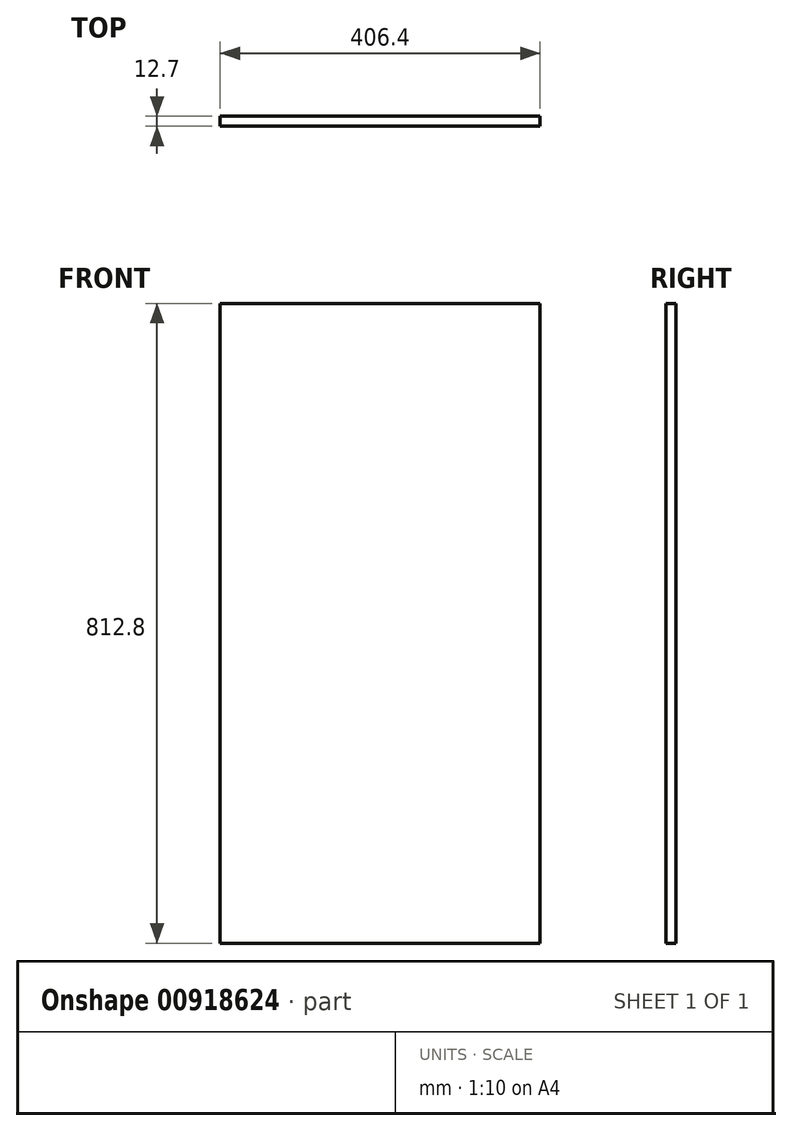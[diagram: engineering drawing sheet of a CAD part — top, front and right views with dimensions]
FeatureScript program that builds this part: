
annotation { "Feature Type Name" : "Feature", "Feature Type Description" : "" }
export const myFeature = defineFeature(function(context is Context, id is Id, definition is map)
    precondition{}
    {
        {
            var Q0;
            Q0=qCreatedBy(makeId("Front.planeOp"),FACE);
            var sketch = newSketch(context, id + "F0", { "sketchPlane" : qUnion([Q0])});
            skLineSegment(sketch, "E0.bottom", {"start": v(-203.2, 406.4) * mm, "end": v(203.2, 406.4) * mm});
            skLineSegment(sketch, "E0.top", {"start": v(-203.2, -406.4) * mm, "end": v(203.2, -406.4) * mm});
            skLineSegment(sketch, "E0.left", {"start": v(-203.2, 406.4) * mm, "end": v(-203.2, -406.4) * mm});
            skLineSegment(sketch, "E0.right", {"start": v(203.2, 406.4) * mm, "end": v(203.2, -406.4) * mm});
            skLineSegment(sketch, "E1", {"start": v(-203.2, 406.4) * mm, "end": v(203.2, -406.4) * mm, "construction": true});
            skSolve(sketch);
        }
        {
            var Q0;
            Q0=makeQuery(id+"F0.imprint","IMPRINT",FACE,{"disambiguationData":[TD([[makeQuery(id+"F0.imprint","IMPRINT",EDGE,{"derivedFrom":sQuery(id+"F0.wireOp",EDGE,"E0.bottom")}),-1.0]])]});
            extrude(context, id + "F1", {"entities" : qUnion([Q0]), "depth" : 12.7 * mm, "offsetDistance" : 25.4 * mm});
        }
    });
